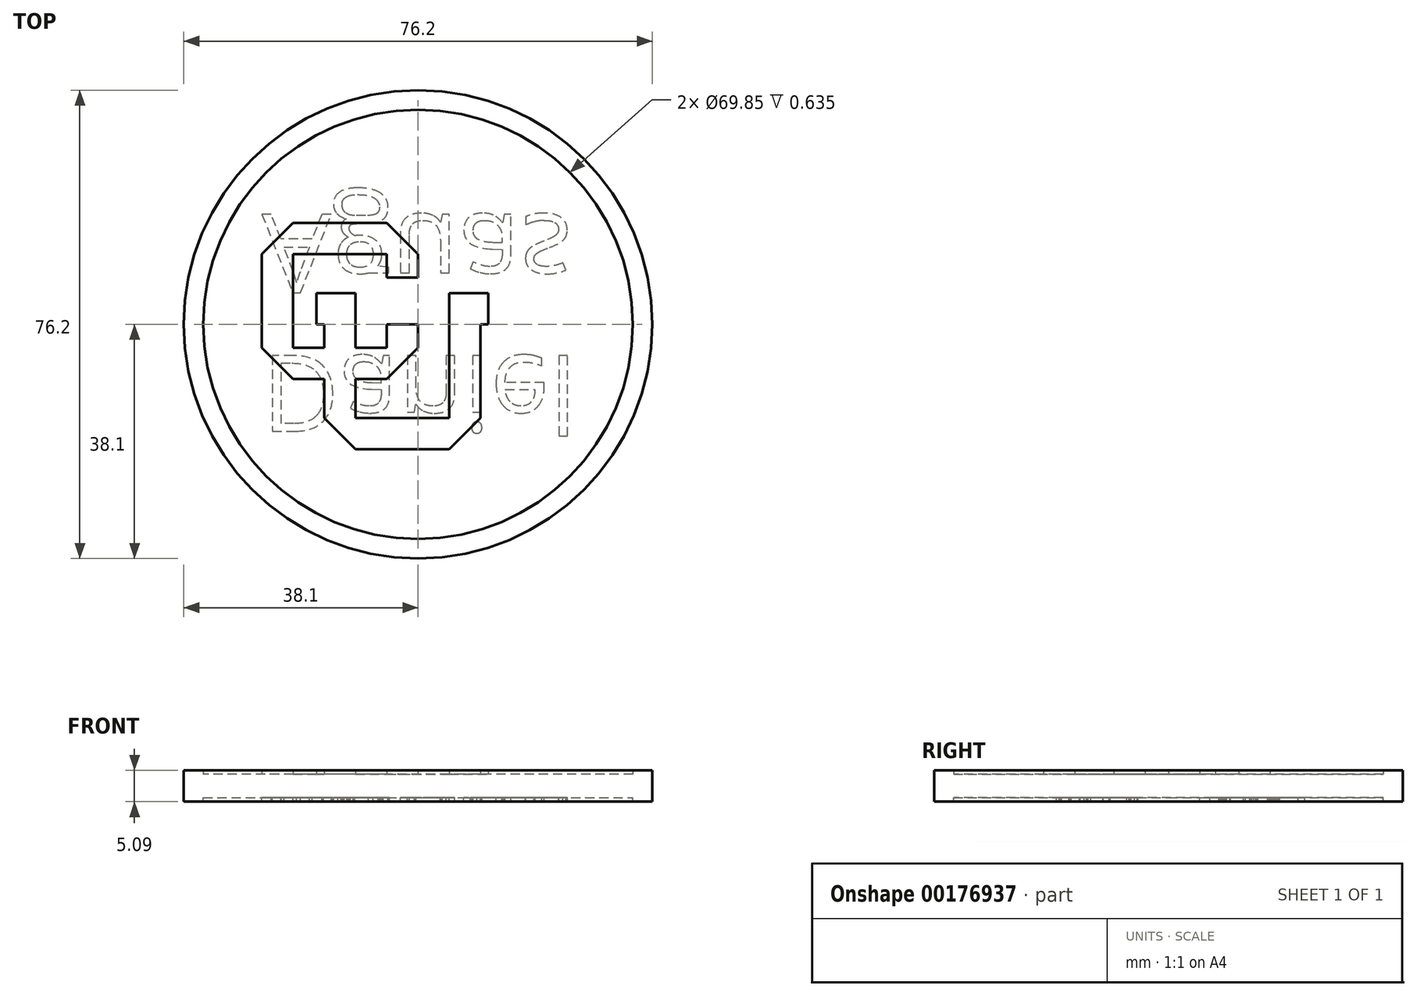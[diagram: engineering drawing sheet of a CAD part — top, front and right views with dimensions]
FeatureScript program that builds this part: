
annotation { "Feature Type Name" : "Feature", "Feature Type Description" : "" }
export const myFeature = defineFeature(function(context is Context, id is Id, definition is map)
    precondition{}
    {
        {
            var Q0;
            Q0=qCreatedBy(makeId("Top.planeOp"),FACE);
            var sketch = newSketch(context, id + "F0", { "sketchPlane" : qUnion([Q0])});
            skCircle(sketch, "E0", {"center": v(0, 0) * mm, "radius": 38.1 * mm});
            skSolve(sketch);
        }
        {
            var Q0;
            Q0=makeQuery(id+"F0.imprint","IMPRINT",FACE,{"disambiguationData":[TD([[makeQuery(id+"F0.imprint","IMPRINT",EDGE,{"derivedFrom":sQuery(id+"F0.wireOp",EDGE,"E0")}),1.0]])]});
            extrude(context, id + "F1", {"entities" : qUnion([Q0]), "depth" : 3.8 * mm});
        }
        {
            var Q0;
            Q0=makeQuery(id+"F1.opExtrude","CAP_FACE",FACE,{"disambiguationData":[OSD([sQuery(id+"F0.wireOp",EDGE,"E0")])],"isStart":false});
            var sketch = newSketch(context, id + "F2", { "sketchPlane" : qUnion([Q0])});
            skSolve(sketch);
        }
        {
            var Q0;
            Q0=makeQuery(id+"F2.imprint","IMPRINT",FACE,{"disambiguationData":[TD([[makeQuery(id+"F2.imprint","IMPRINT",EDGE,{"derivedFrom":makeQuery(id+"F1.opExtrude","CAP_EDGE",EDGE,{"disambiguationData":[OSD([sQuery(id+"F0.wireOp",EDGE,"E0")])],"isStart":false})}),1.0]])]});
            var sketch = newSketch(context, id + "F3", { "sketchPlane" : qUnion([Q0])});
            skLineSegment(sketch, "E1", {"start": v(0, 0) * mm, "end": v(0, -3.81) * mm});
            skLineSegment(sketch, "E2", {"start": v(0, -3.8) * mm, "end": v(-5.08, -8.9) * mm});
            skLineSegment(sketch, "E3", {"start": v(-5.08, -8.9) * mm, "end": v(-10.16, -8.9) * mm});
            skLineSegment(sketch, "E4", {"start": v(-20.32, -8.9) * mm, "end": v(-25.4, -3.81) * mm});
            skLineSegment(sketch, "E5", {"start": v(-25.4, -3.81) * mm, "end": v(-25.4, 11.43) * mm});
            skLineSegment(sketch, "E6", {"start": v(-25.4, 11.43) * mm, "end": v(-20.32, 16.5) * mm});
            skLineSegment(sketch, "E7", {"start": v(-20.32, 16.5) * mm, "end": v(-5.08, 16.5) * mm});
            skLineSegment(sketch, "E8", {"start": v(-5.08, 16.5) * mm, "end": v(0, 11.43) * mm});
            skLineSegment(sketch, "E9", {"start": v(0, 11.43) * mm, "end": v(0, 7.62) * mm});
            skLineSegment(sketch, "E10", {"start": v(0, 7.62) * mm, "end": v(-5.08, 7.62) * mm});
            skLineSegment(sketch, "E11", {"start": v(-5.08, 7.62) * mm, "end": v(-5.08, 11.43) * mm});
            skLineSegment(sketch, "E12", {"start": v(-5.08, 11.43) * mm, "end": v(-20.32, 11.43) * mm});
            skLineSegment(sketch, "E13", {"start": v(-20.32, 11.43) * mm, "end": v(-20.32, -3.81) * mm});
            skLineSegment(sketch, "E14", {"start": v(-20.32, -3.81) * mm, "end": v(-15.24, -3.81) * mm});
            skLineSegment(sketch, "E15", {"start": v(-5.08, -3.81) * mm, "end": v(-5.08, 0) * mm});
            skLineSegment(sketch, "E16", {"start": v(-5.08, 0) * mm, "end": v(0, 0) * mm});
            skLineSegment(sketch, "E17", {"start": v(-10.16, -3.81) * mm, "end": v(-10.16, 5.08) * mm});
            skLineSegment(sketch, "E18", {"start": v(-10.16, 5.08) * mm, "end": v(-16.51, 5.08) * mm});
            skLineSegment(sketch, "E19", {"start": v(-16.51, 5.08) * mm, "end": v(-16.51, 0) * mm});
            skLineSegment(sketch, "E20", {"start": v(-16.51, 0) * mm, "end": v(-15.24, 0) * mm});
            skLineSegment(sketch, "E21", {"start": v(-15.24, 0) * mm, "end": v(-15.24, -3.81) * mm});
            skLineSegment(sketch, "E22", {"start": v(-15.24, -8.9) * mm, "end": v(-15.24, -15.24) * mm});
            skLineSegment(sketch, "E23", {"start": v(-10.16, -8.9) * mm, "end": v(-10.16, -15.24) * mm});
            skLineSegment(sketch, "E24", {"start": v(-10.16, -15.24) * mm, "end": v(5.08, -15.24) * mm});
            skLineSegment(sketch, "E25", {"start": v(5.08, 5.08) * mm, "end": v(11.43, 5.08) * mm});
            skLineSegment(sketch, "E26", {"start": v(11.43, 5.08) * mm, "end": v(5.08, 5.08) * mm});
            skLineSegment(sketch, "E27", {"start": v(5.08, -15.24) * mm, "end": v(5.08, 5.08) * mm});
            skLineSegment(sketch, "E28", {"start": v(11.43, 5.08) * mm, "end": v(11.43, 0) * mm});
            skLineSegment(sketch, "E29", {"start": v(11.43, 0) * mm, "end": v(10.16, 0) * mm});
            skLineSegment(sketch, "E30", {"start": v(10.16, 0) * mm, "end": v(10.16, -15.24) * mm});
            skLineSegment(sketch, "E31", {"start": v(10.16, -15.24) * mm, "end": v(5.08, -20.32) * mm});
            skLineSegment(sketch, "E32", {"start": v(5.08, -20.32) * mm, "end": v(-10.16, -20.32) * mm});
            skLineSegment(sketch, "E33", {"start": v(-10.16, -20.32) * mm, "end": v(-15.24, -15.24) * mm});
            skLineSegment(sketch, "E34.trimOffspring", {"start": v(-10.16, -3.81) * mm, "end": v(-5.08, -3.81) * mm});
            skLineSegment(sketch, "E35.trimOffspring", {"start": v(-15.24, -8.9) * mm, "end": v(-20.32, -8.9) * mm});
            skCircle(sketch, "E36", {"center": v(0, 0) * mm, "radius": 38.1 * mm});
            skCircle(sketch, "E37.0", {"center": v(0, 0) * mm, "radius": 34.93 * mm});
            skSolve(sketch);
        }
        {
            var Q0;
            Q0 = qSketchRegion(id + "F3", true);
            var Q1;
            Q1=makeQuery(id+"F3.imprint","IMPRINT",FACE,{"disambiguationData":[TD([[makeQuery(id+"F3.imprint","IMPRINT",EDGE,{"derivedFrom":sQuery(id+"F3.wireOp",EDGE,"E1")}),-1.0]])]});
            extrude(context, id + "F4", {"entities" : qUnion([Q0, Q1]), "operationType" : NewBodyOperationType.ADD, "depth" : 0.64 * mm});
        }
        {
            var Q0;
            Q0=makeQuery(id+"F1.opExtrude","CAP_FACE",FACE,{"disambiguationData":[OSD([sQuery(id+"F0.wireOp",EDGE,"E0")])],"isStart":true});
            var sketch = newSketch(context, id + "F5", { "sketchPlane" : qUnion([Q0])});
            skSolve(sketch);
        }
        {
            var Q0;
            Q0=makeQuery(id+"F5.imprint","IMPRINT",FACE,{"disambiguationData":[TD([[makeQuery(id+"F5.imprint","IMPRINT",EDGE,{"derivedFrom":makeQuery(id+"F1.opExtrude","CAP_EDGE",EDGE,{"disambiguationData":[OSD([sQuery(id+"F0.wireOp",EDGE,"E0")])],"isStart":true})}),-1.0]])]});
            var sketch = newSketch(context, id + "F6", { "sketchPlane" : qUnion([Q0])});
            skText(sketch, "E38", { "text": "Daniel", "fontName": "OpenSans-Regular.ttf"});
            skText(sketch, "E39", { "text": "Aguas", "fontName": "OpenSans-Regular.ttf"});
            skCircle(sketch, "E40", {"center": v(0, 0) * mm, "radius": 38.1 * mm});
            skCircle(sketch, "E41.0", {"center": v(0, 0) * mm, "radius": 34.93 * mm});
            const initialGuessF6  = {"E38": [-0.0254, 0.00508, 1, 0, 0.01242], "E39": [-0.0254, -0.01793, 1, 0, 0.01285]};
            skSetInitialGuess(sketch, initialGuessF6);
            skSolve(sketch);
        }
        {
            var Q0;
            Q0=makeQuery(id+"F6.imprint","IMPRINT",FACE,{"disambiguationData":[TD([[makeQuery(id+"F6.imprint","IMPRINT",EDGE,{"derivedFrom":sQuery(id+"F6.wireOp",EDGE,"E38.sketch_text.stroke-14")}),-1.0]])]});
            var Q1;
            Q1=makeQuery(id+"F6.imprint","IMPRINT",FACE,{"disambiguationData":[TD([[makeQuery(id+"F6.imprint","IMPRINT",EDGE,{"derivedFrom":sQuery(id+"F6.wireOp",EDGE,"E38.sketch_text.stroke-41")}),-1.0]])]});
            var Q2;
            Q2=makeQuery(id+"F6.imprint","IMPRINT",FACE,{"disambiguationData":[TD([[makeQuery(id+"F6.imprint","IMPRINT",EDGE,{"derivedFrom":sQuery(id+"F6.wireOp",EDGE,"E40")}),-1.0]])]});
            var Q3;
            Q3=makeQuery(id+"F6.imprint","IMPRINT",FACE,{"disambiguationData":[TD([[makeQuery(id+"F6.imprint","IMPRINT",EDGE,{"derivedFrom":sQuery(id+"F6.wireOp",EDGE,"E38.sketch_text.stroke-0")}),-1.0]])]});
            var Q4;
            Q4=makeQuery(id+"F6.imprint","IMPRINT",FACE,{"disambiguationData":[TD([[makeQuery(id+"F6.imprint","IMPRINT",EDGE,{"derivedFrom":sQuery(id+"F6.wireOp",EDGE,"E38.sketch_text.stroke-62")}),-1.0]])]});
            var Q5;
            Q5=makeQuery(id+"F6.imprint","IMPRINT",FACE,{"disambiguationData":[TD([[makeQuery(id+"F6.imprint","IMPRINT",EDGE,{"derivedFrom":sQuery(id+"F6.wireOp",EDGE,"E38.sketch_text.stroke-58")}),-1.0]])]});
            var Q6;
            Q6=makeQuery(id+"F6.imprint","IMPRINT",FACE,{"disambiguationData":[TD([[makeQuery(id+"F6.imprint","IMPRINT",EDGE,{"derivedFrom":sQuery(id+"F6.wireOp",EDGE,"E38.sketch_text.stroke-70")}),-1.0]])]});
            var Q7;
            Q7=makeQuery(id+"F6.imprint","IMPRINT",FACE,{"disambiguationData":[TD([[makeQuery(id+"F6.imprint","IMPRINT",EDGE,{"derivedFrom":sQuery(id+"F6.wireOp",EDGE,"E38.sketch_text.stroke-89")}),-1.0]])]});
            var Q8;
            Q8=makeQuery(id+"F6.imprint","IMPRINT",FACE,{"disambiguationData":[TD([[makeQuery(id+"F6.imprint","IMPRINT",EDGE,{"derivedFrom":sQuery(id+"F6.wireOp",EDGE,"E39.sketch_text.stroke-101")}),-1.0]])]});
            var Q9;
            Q9=makeQuery(id+"F6.imprint","IMPRINT",FACE,{"disambiguationData":[TD([[makeQuery(id+"F6.imprint","IMPRINT",EDGE,{"derivedFrom":sQuery(id+"F6.wireOp",EDGE,"E39.sketch_text.stroke-74")}),-1.0]])]});
            var Q10;
            Q10=makeQuery(id+"F6.imprint","IMPRINT",FACE,{"disambiguationData":[TD([[makeQuery(id+"F6.imprint","IMPRINT",EDGE,{"derivedFrom":sQuery(id+"F6.wireOp",EDGE,"E39.sketch_text.stroke-57")}),-1.0]])]});
            var Q11;
            Q11=makeQuery(id+"F6.imprint","IMPRINT",FACE,{"disambiguationData":[TD([[makeQuery(id+"F6.imprint","IMPRINT",EDGE,{"derivedFrom":sQuery(id+"F6.wireOp",EDGE,"E39.sketch_text.stroke-13")}),-1.0]])]});
            var Q12;
            Q12=makeQuery(id+"F6.imprint","IMPRINT",FACE,{"disambiguationData":[TD([[makeQuery(id+"F6.imprint","IMPRINT",EDGE,{"derivedFrom":sQuery(id+"F6.wireOp",EDGE,"E39.sketch_text.stroke-0")}),-1.0]])]});
            extrude(context, id + "F7", {"entities" : qUnion([Q0, Q1, Q2, Q3, Q4, Q5, Q6, Q7, Q8, Q9, Q10, Q11, Q12]), "operationType" : NewBodyOperationType.ADD, "depth" : 0.64 * mm});
        }
    });
